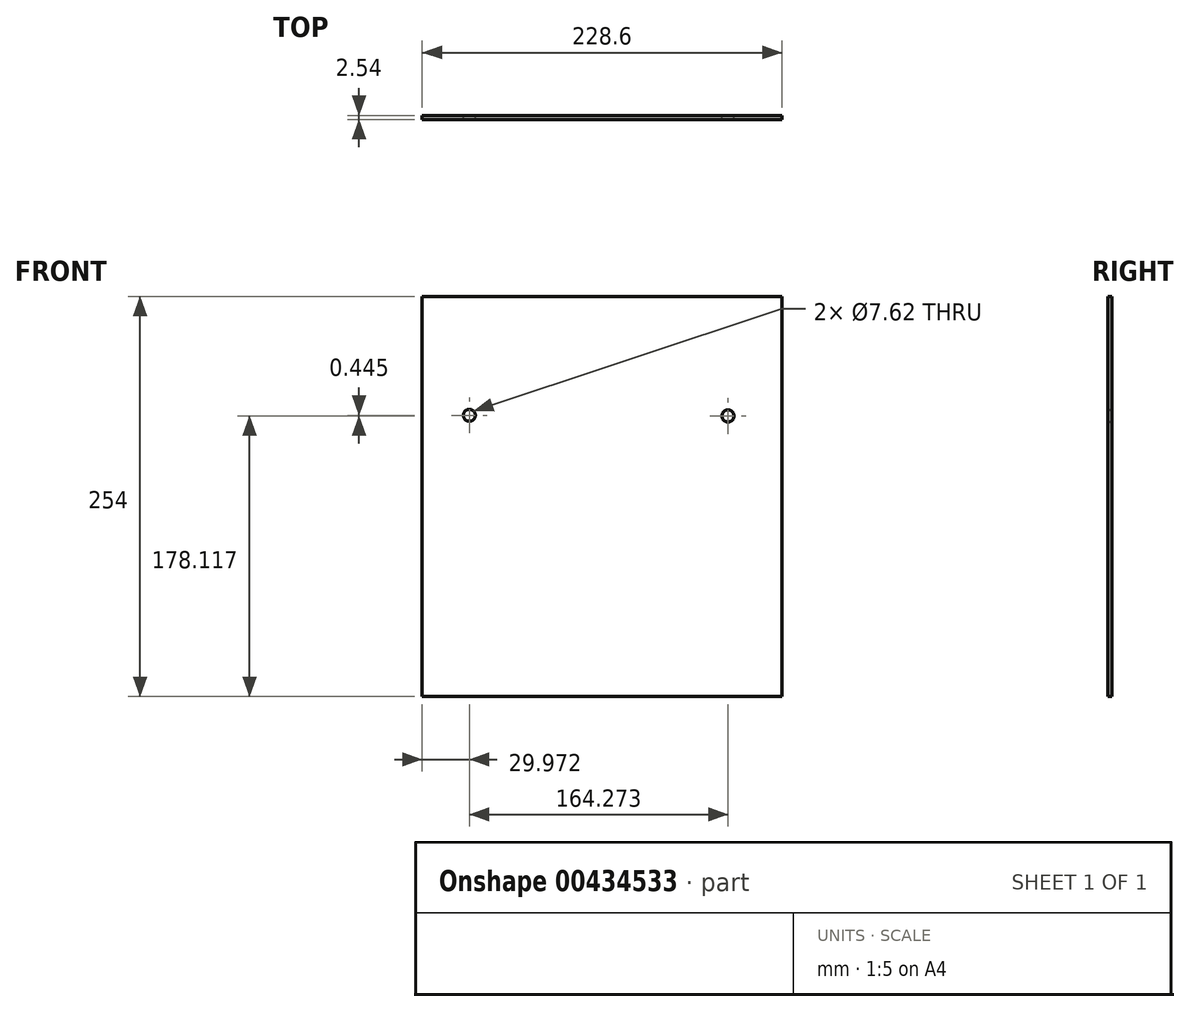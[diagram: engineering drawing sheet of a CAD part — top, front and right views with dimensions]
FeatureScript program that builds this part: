
annotation { "Feature Type Name" : "Feature", "Feature Type Description" : "" }
export const myFeature = defineFeature(function(context is Context, id is Id, definition is map)
    precondition{}
    {
        {
            var Q0;
            Q0=qCreatedBy(makeId("Front.planeOp"),FACE);
            var sketch = newSketch(context, id + "F0", { "sketchPlane" : qUnion([Q0])});
            skLineSegment(sketch, "E0.bottom", {"start": v(-114.3, 127) * mm, "end": v(114.3, 127) * mm});
            skLineSegment(sketch, "E0.top", {"start": v(-114.3, -127) * mm, "end": v(114.3, -127) * mm});
            skLineSegment(sketch, "E0.left", {"start": v(-114.3, 127) * mm, "end": v(-114.3, -127) * mm});
            skLineSegment(sketch, "E0.right", {"start": v(114.3, 127) * mm, "end": v(114.3, -127) * mm});
            skPoint(sketch, "E0.middle", {"position": v(0, 0) * mm});
            skSolve(sketch);
        }
        {
            var Q0;
            Q0 = qSketchRegion(id + "F0", true);
            extrude(context, id + "F1", {"entities" : qUnion([Q0]), "depth" : 2.54 * mm});
        }
        {
            var Q0;
            Q0=makeQuery(id+"F1.opExtrude","CAP_FACE",FACE,{"disambiguationData":[OSD([sQuery(id+"F0.wireOp",EDGE,"E0.bottom"),sQuery(id+"F0.wireOp",EDGE,"E0.top"),sQuery(id+"F0.wireOp",EDGE,"E0.left"),sQuery(id+"F0.wireOp",EDGE,"E0.right")])],"isStart":true});
            var sketch = newSketch(context, id + "F2", { "sketchPlane" : qUnion([Q0])});
            skCircle(sketch, "E1", {"center": v(84.33, 51.56) * mm, "radius": 3.81 * mm});
            skCircle(sketch, "E2", {"center": v(-79.94, 51.12) * mm, "radius": 3.81 * mm});
            skSolve(sketch);
        }
        {
            var Q0;
            Q0=sQuery(id+"F2.wireOp",VERTEX,"E2.center");
            var Q1;
            Q1=sQuery(id+"F2.wireOp",VERTEX,"E1.center");
            var Q2;
            Q2=makeQuery(id+"F1.opExtrude","SWEPT_BODY",BODY,{"disambiguationData":[OSD([sQuery(id+"F0.wireOp",EDGE,"E0.bottom"),sQuery(id+"F0.wireOp",EDGE,"E0.top"),sQuery(id+"F0.wireOp",EDGE,"E0.left"),sQuery(id+"F0.wireOp",EDGE,"E0.right")])]});
            hole(context, id + "F3", {"style" : HoleStyle.SIMPLE, "endStyle" : HoleEndStyle.THROUGH, "holeDiameter" : 7.62 * mm, "isTappedThrough" : true, "tappedDepth" : 12.7 * mm, "tapClearance" : 3, "locations" : qUnion([Q0, Q1]), "scope" : qUnion([Q2])});
        }
    });
